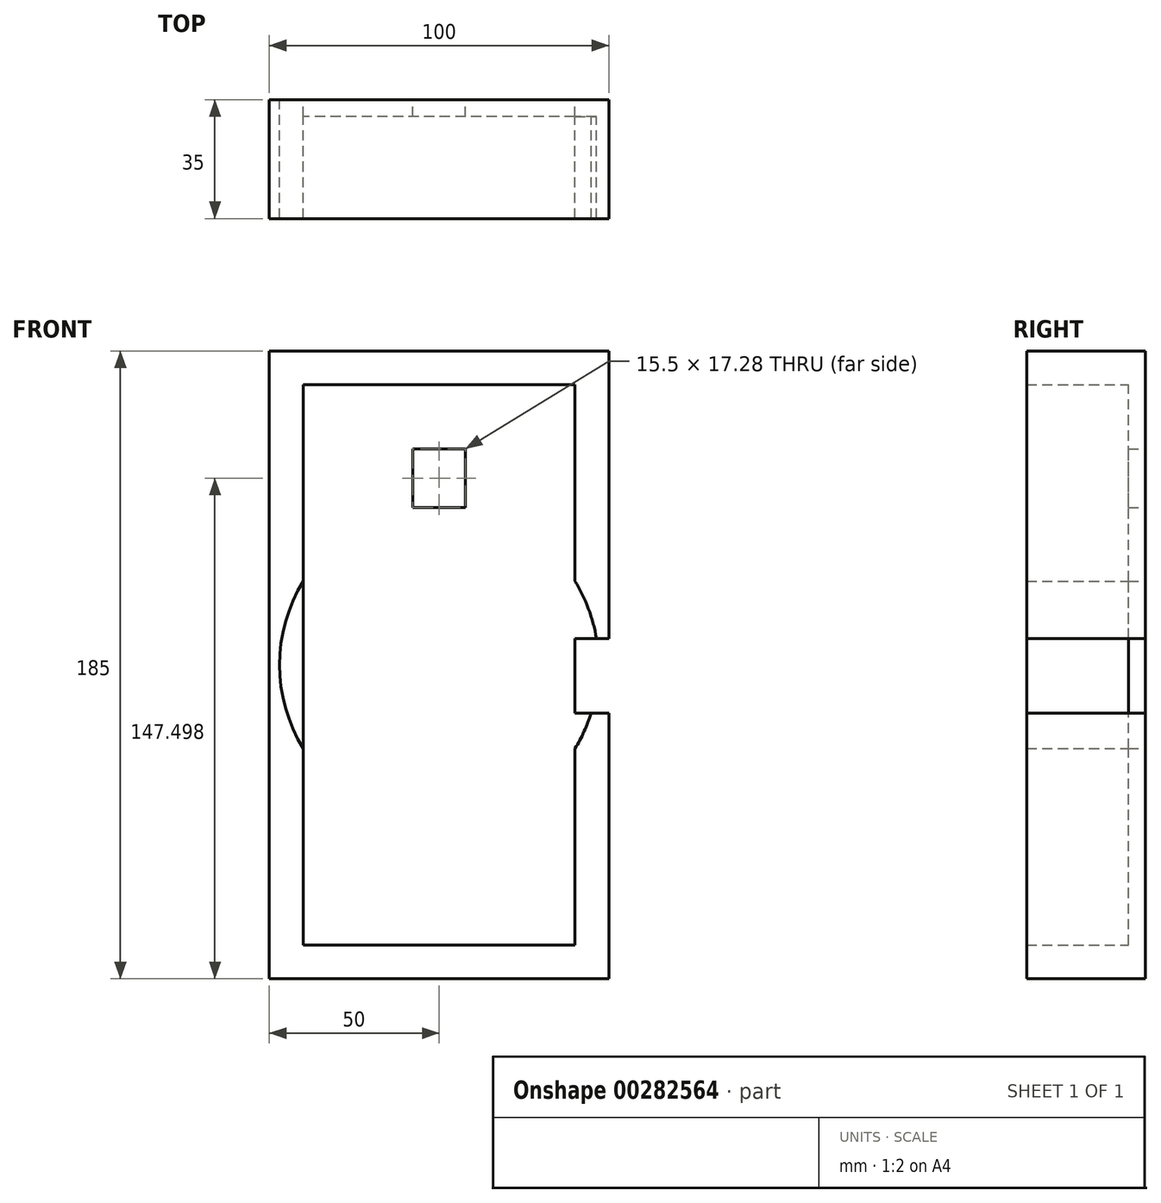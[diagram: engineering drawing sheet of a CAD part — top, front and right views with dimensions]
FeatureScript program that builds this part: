
annotation { "Feature Type Name" : "Feature", "Feature Type Description" : "" }
export const myFeature = defineFeature(function(context is Context, id is Id, definition is map)
    precondition{}
    {
        {
            var Q0;
            Q0=qCreatedBy(makeId("Front.planeOp"),FACE);
            var sketch = newSketch(context, id + "F0", { "sketchPlane" : qUnion([Q0])});
            skLineSegment(sketch, "E0.bottom", {"start": v(40, -82.5) * mm, "end": v(-40, -82.5) * mm});
            skLineSegment(sketch, "E0.top", {"start": v(40, 82.5) * mm, "end": v(-40, 82.5) * mm});
            skLineSegment(sketch, "E0.left", {"start": v(40, -82.5) * mm, "end": v(40, 82.5) * mm});
            skLineSegment(sketch, "E0.right", {"start": v(-40, -82.5) * mm, "end": v(-40, 82.5) * mm});
            skPoint(sketch, "E0.middle", {"position": v(0, 0) * mm});
            skCircle(sketch, "E1", {"center": v(0, 0) * mm, "radius": 47 * mm});
            skLineSegment(sketch, "E2.bottom", {"start": v(50, -92.5) * mm, "end": v(-50, -92.5) * mm});
            skLineSegment(sketch, "E2.top", {"start": v(50, 92.5) * mm, "end": v(-50, 92.5) * mm});
            skLineSegment(sketch, "E2.left", {"start": v(50, -92.5) * mm, "end": v(50, 92.5) * mm});
            skLineSegment(sketch, "E2.right", {"start": v(-50, -92.5) * mm, "end": v(-50, 92.5) * mm});
            skLineSegment(sketch, "E3.bottom", {"start": v(40, -14.21) * mm, "end": v(75.52, -14.21) * mm});
            skLineSegment(sketch, "E3.top", {"start": v(40, 7.79) * mm, "end": v(75.52, 7.79) * mm});
            skLineSegment(sketch, "E3.left", {"start": v(40, -14.21) * mm, "end": v(40, 7.79) * mm});
            skLineSegment(sketch, "E3.right", {"start": v(75.52, -14.21) * mm, "end": v(75.52, 7.79) * mm});
            skPoint(sketch, "E4", {"position": v(0, 55) * mm});
            skLineSegment(sketch, "E5.bottom", {"start": v(7.75, 46.36) * mm, "end": v(-7.75, 46.36) * mm});
            skLineSegment(sketch, "E5.top", {"start": v(7.75, 63.64) * mm, "end": v(-7.75, 63.64) * mm});
            skLineSegment(sketch, "E5.left", {"start": v(7.75, 46.36) * mm, "end": v(7.75, 63.64) * mm});
            skLineSegment(sketch, "E5.right", {"start": v(-7.75, 46.36) * mm, "end": v(-7.75, 63.64) * mm});
            skSolve(sketch);
        }
        {
            var Q0;
            {var subQ5=sQuery(id+"F0.wireOp",EDGE,"E0.bottom");Q0=makeQuery(id+"F0.imprint","IMPRINT",FACE,{"disambiguationData":[TD([[makeQuery(id+"F0.imprint","IMPRINT",EDGE,{"derivedFrom":subQ5}),1.0]])]});}
            extrude(context, id + "F1", {"entities" : qUnion([Q0]), "depth" : 35 * mm});
        }
        {
            var Q0;
            {var subQ0=sQuery(id+"F0.wireOp",EDGE,"E1");var subQ1=sQuery(id+"F0.wireOp",EDGE,"E0.left");var subQ2=makeQuery(id+"F0.imprint","INTERSECT",VERTEX,{"disambiguationData":[OD(0.0)],"derivedFrom":[subQ1,subQ0]});Q0=makeQuery(id+"F0.imprint","IMPRINT",FACE,{"disambiguationData":[TD([[makeQuery(id+"F0.imprint","IMPRINT",EDGE,{"disambiguationData":[TD([[subQ2,-1.0]])],"derivedFrom":subQ1}),1.0]])]});}
            var Q1;
            {var subQ0=sQuery(id+"F0.wireOp",EDGE,"E0.bottom");Q1=makeQuery(id+"F0.imprint","IMPRINT",FACE,{"disambiguationData":[TD([[makeQuery(id+"F0.imprint","IMPRINT",EDGE,{"derivedFrom":subQ0}),-1.0]])]});}
            var Q2;
            {var subQ0=sQuery(id+"F0.wireOp",EDGE,"E1");var subQ1=sQuery(id+"F0.wireOp",EDGE,"E0.left");var subQ2=makeQuery(id+"F0.imprint","INTERSECT",VERTEX,{"disambiguationData":[OD(0.0)],"derivedFrom":[subQ1,subQ0]});Q2=makeQuery(id+"F0.imprint","IMPRINT",FACE,{"disambiguationData":[TD([[makeQuery(id+"F0.imprint","IMPRINT",EDGE,{"disambiguationData":[TD([[subQ2,-1.0]])],"derivedFrom":subQ1}),-1.0]])]});}
            var Q3;
            {var subQ0=sQuery(id+"F0.wireOp",EDGE,"E0.top");Q3=makeQuery(id+"F0.imprint","IMPRINT",FACE,{"disambiguationData":[TD([[makeQuery(id+"F0.imprint","IMPRINT",EDGE,{"derivedFrom":subQ0}),1.0]])]});}
            var Q4;
            {var subQ0=sQuery(id+"F0.wireOp",EDGE,"E1");var subQ1=sQuery(id+"F0.wireOp",EDGE,"E0.right");var subQ2=makeQuery(id+"F0.imprint","INTERSECT",VERTEX,{"disambiguationData":[OD(0.0)],"derivedFrom":[subQ1,subQ0]});Q4=makeQuery(id+"F0.imprint","IMPRINT",FACE,{"disambiguationData":[TD([[makeQuery(id+"F0.imprint","IMPRINT",EDGE,{"disambiguationData":[TD([[subQ2,-1.0]])],"derivedFrom":subQ1}),1.0]])]});}
            var Q5;
            {var subQ1=sQuery(id+"F0.wireOp",EDGE,"E0.left");var subQ3=sQuery(id+"F0.wireOp",EDGE,"E1");var subQ4=makeQuery(id+"F0.imprint","INTERSECT",VERTEX,{"disambiguationData":[OD(1.0)],"derivedFrom":[subQ1,subQ3]});Q5=makeQuery(id+"F0.imprint","IMPRINT",FACE,{"disambiguationData":[TD([[makeQuery(id+"F0.imprint","IMPRINT",EDGE,{"disambiguationData":[TD([[subQ4,1.0]])],"derivedFrom":subQ3}),1.0]])]});}
            var Q6;
            {var subQ5=sQuery(id+"F0.wireOp",EDGE,"E3.left");Q6=makeQuery(id+"F0.imprint","IMPRINT",FACE,{"disambiguationData":[TD([[makeQuery(id+"F0.imprint","IMPRINT",EDGE,{"derivedFrom":subQ5}),-1.0]])]});}
            extrude(context, id + "F2", {"entities" : qUnion([Q0, Q1, Q2, Q3, Q4, Q5, Q6]), "operationType" : NewBodyOperationType.ADD, "depth" : 5 * mm});
        }
    });
